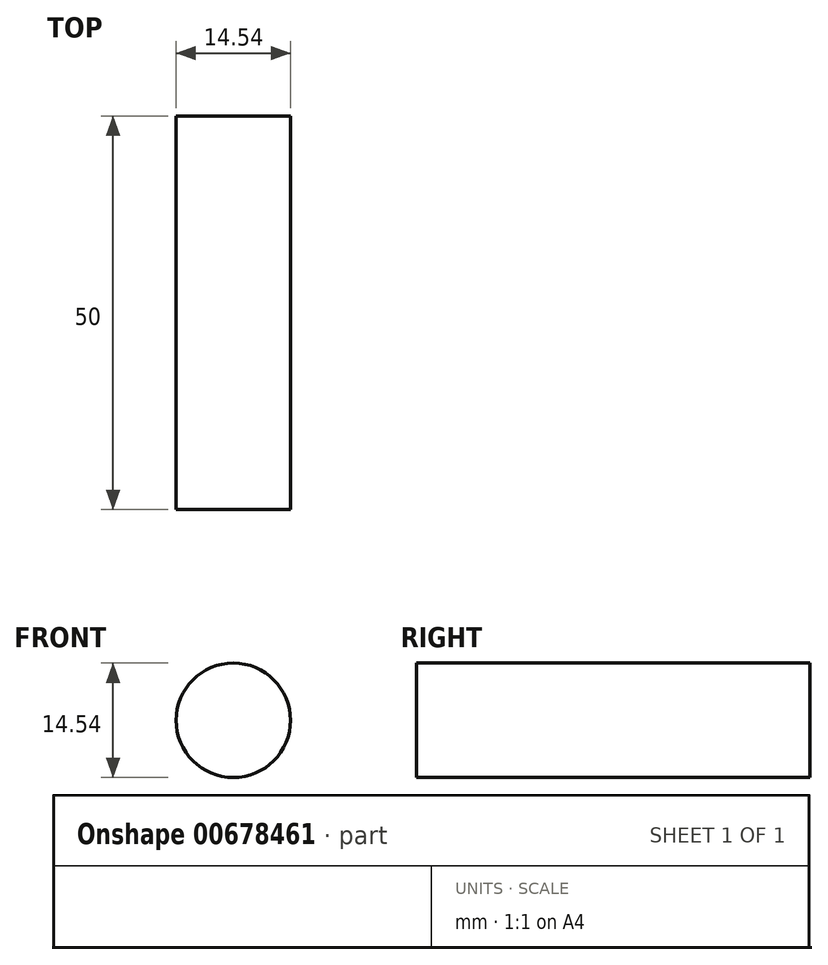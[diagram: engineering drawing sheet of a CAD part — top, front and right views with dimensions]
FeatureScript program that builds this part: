
annotation { "Feature Type Name" : "Feature", "Feature Type Description" : "" }
export const myFeature = defineFeature(function(context is Context, id is Id, definition is map)
    precondition{}
    {
        {
            var Q0;
            Q0=qCreatedBy(makeId("Front.planeOp"),FACE);
            var sketch = newSketch(context, id + "F0", { "sketchPlane" : qUnion([Q0])});
            skCircle(sketch, "E0", {"center": v(0, 0) * mm, "radius": 7.27 * mm});
            skSolve(sketch);
        }
        {
            var Q0;
            Q0=makeQuery(id+"F0.imprint","IMPRINT",FACE,{"disambiguationData":[TD([[makeQuery(id+"F0.imprint","IMPRINT",EDGE,{"derivedFrom":sQuery(id+"F0.wireOp",EDGE,"E0")}),1.0]])]});
            extrude(context, id + "F1", {"entities" : qUnion([Q0]), "depth" : 50 * mm, "offsetDistance" : 25 * mm});
        }
    });
